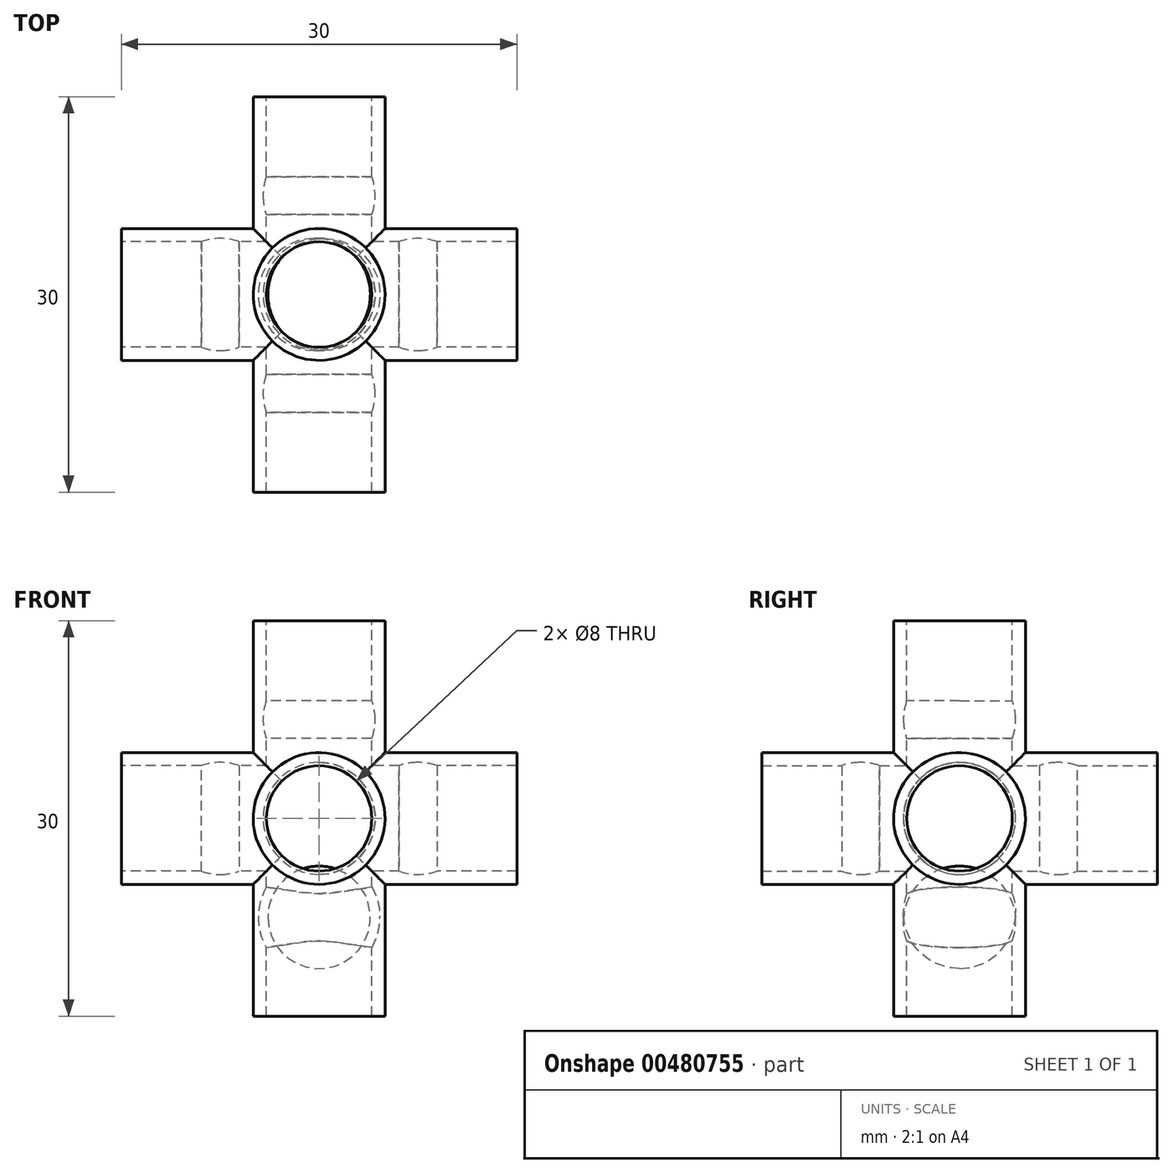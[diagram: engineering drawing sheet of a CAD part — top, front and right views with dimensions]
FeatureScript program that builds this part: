
annotation { "Feature Type Name" : "Feature", "Feature Type Description" : "" }
export const myFeature = defineFeature(function(context is Context, id is Id, definition is map)
    precondition{}
    {
        {
            var Q0;
            Q0=qCreatedBy(makeId("Top.planeOp"),FACE);
            var sketch = newSketch(context, id + "F0", { "sketchPlane" : qUnion([Q0])});
            skCircle(sketch, "E0", {"center": v(0, 0) * mm, "radius": 5 * mm});
            skSolve(sketch);
        }
        {
            var Q0;
            Q0=qCreatedBy(makeId("Right.planeOp"),FACE);
            var sketch = newSketch(context, id + "F1", { "sketchPlane" : qUnion([Q0])});
            skCircle(sketch, "E1", {"center": v(0, 0) * mm, "radius": 5 * mm});
            skSolve(sketch);
        }
        {
            var Q0;
            Q0=qCreatedBy(makeId("Front.planeOp"),FACE);
            var sketch = newSketch(context, id + "F2", { "sketchPlane" : qUnion([Q0])});
            skCircle(sketch, "E2", {"center": v(0, 0) * mm, "radius": 5 * mm});
            skSolve(sketch);
        }
        {
            var Q0;
            Q0 = qSketchRegion(id + "F0", true);
            extrude(context, id + "F3", {"entities" : qUnion([Q0]), "endBound" : BoundingType.SYMMETRIC, "depth" : 30 * mm});
        }
        {
            var Q0;
            Q0 = qSketchRegion(id + "F1", true);
            extrude(context, id + "F4", {"entities" : qUnion([Q0]), "operationType" : NewBodyOperationType.ADD, "endBound" : BoundingType.SYMMETRIC, "depth" : 30 * mm});
        }
        {
            var Q0;
            Q0 = qSketchRegion(id + "F2", true);
            extrude(context, id + "F5", {"entities" : qUnion([Q0]), "operationType" : NewBodyOperationType.ADD, "endBound" : BoundingType.SYMMETRIC, "depth" : 30 * mm});
        }
        {
            var Q0;
            Q0=qCreatedBy(makeId("Top.planeOp"),FACE);
            var sketch = newSketch(context, id + "F6", { "sketchPlane" : qUnion([Q0])});
            skCircle(sketch, "E3", {"center": v(0, 0) * mm, "radius": 4 * mm});
            skSolve(sketch);
        }
        {
            var Q0;
            Q0=qCreatedBy(makeId("Right.planeOp"),FACE);
            var sketch = newSketch(context, id + "F7", { "sketchPlane" : qUnion([Q0])});
            skCircle(sketch, "E4", {"center": v(0, 0) * mm, "radius": 4 * mm});
            skSolve(sketch);
        }
        {
            var Q0;
            Q0=qCreatedBy(makeId("Front.planeOp"),FACE);
            var sketch = newSketch(context, id + "F8", { "sketchPlane" : qUnion([Q0])});
            skCircle(sketch, "E5", {"center": v(0, 0) * mm, "radius": 4 * mm});
            skSolve(sketch);
        }
        {
            var Q0;
            Q0 = qSketchRegion(id + "F6", true);
            extrude(context, id + "F9", {"entities" : qUnion([Q0]), "operationType" : NewBodyOperationType.REMOVE, "endBound" : BoundingType.SYMMETRIC, "oppositeDirection" : true, "depth" : 30 * mm});
        }
        {
            var Q0;
            Q0 = qSketchRegion(id + "F7", true);
            extrude(context, id + "F10", {"entities" : qUnion([Q0]), "operationType" : NewBodyOperationType.REMOVE, "endBound" : BoundingType.SYMMETRIC, "depth" : 30 * mm});
        }
        {
            var Q0;
            Q0 = qSketchRegion(id + "F8", true);
            extrude(context, id + "F11", {"entities" : qUnion([Q0]), "operationType" : NewBodyOperationType.REMOVE, "endBound" : BoundingType.SYMMETRIC, "depth" : 30 * mm});
        }
        {
            var Q0;
            Q0=qCreatedBy(makeId("Front.planeOp"),FACE);
            cPlane(context, id + "F12", {"entities" : qUnion([Q0]), "cplaneType" : CPlaneType.OFFSET, "offset" : 7.5 * mm, "width" : 150 * mm, "height" : 150 * mm});
        }
        {
            var Q0;
            Q0=qCreatedBy(makeId("Front.planeOp"),FACE);
            cPlane(context, id + "F13", {"entities" : qUnion([Q0]), "cplaneType" : CPlaneType.OFFSET, "offset" : 7.5 * mm, "oppositeDirection" : true, "width" : 150 * mm, "height" : 150 * mm});
        }
        {
            var Q0;
            Q0=qCreatedBy(makeId("Top.planeOp"),FACE);
            cPlane(context, id + "F14", {"entities" : qUnion([Q0]), "cplaneType" : CPlaneType.OFFSET, "offset" : 7.5 * mm, "width" : 150 * mm, "height" : 150 * mm});
        }
        {
            var Q0;
            Q0=qCreatedBy(makeId("Top.planeOp"),FACE);
            cPlane(context, id + "F15", {"entities" : qUnion([Q0]), "cplaneType" : CPlaneType.OFFSET, "offset" : 7.5 * mm, "oppositeDirection" : true, "width" : 150 * mm, "height" : 150 * mm});
        }
        {
            var Q0;
            Q0=qCreatedBy(makeId("Right.planeOp"),FACE);
            cPlane(context, id + "F16", {"entities" : qUnion([Q0]), "cplaneType" : CPlaneType.OFFSET, "offset" : 7.5 * mm, "width" : 150 * mm, "height" : 150 * mm});
        }
        {
            var Q0;
            Q0=qCreatedBy(makeId("Right.planeOp"),FACE);
            cPlane(context, id + "F17", {"entities" : qUnion([Q0]), "cplaneType" : CPlaneType.OFFSET, "offset" : 7.5 * mm, "oppositeDirection" : true, "width" : 150 * mm, "height" : 150 * mm});
        }
        {
            var Q0;
            Q0=qCreatedBy(id+"F12.planeOp",FACE);
            var sketch = newSketch(context, id + "F18", { "sketchPlane" : qUnion([Q0])});
            skLineSegment(sketch, "E6", {"start": v(0, 4.25) * mm, "end": v(0, -4.25) * mm});
            skArc(sketch, "E7", {"start": v(0, -4.25) * mm, "mid": v(4.25, 0) * mm, "end": v(0, 4.25) * mm});
            skSolve(sketch);
        }
        {
            var Q0;
            Q0=qCreatedBy(id+"F13.planeOp",FACE);
            var sketch = newSketch(context, id + "F19", { "sketchPlane" : qUnion([Q0])});
            skLineSegment(sketch, "E8", {"start": v(0, 4.25) * mm, "end": v(0, -4.25) * mm});
            skArc(sketch, "E9", {"start": v(0, 4.25) * mm, "mid": v(-4.25, 0) * mm, "end": v(0, -4.25) * mm});
            skSolve(sketch);
        }
        {
            var Q0;
            Q0=qCreatedBy(id+"F14.planeOp",FACE);
            var sketch = newSketch(context, id + "F20", { "sketchPlane" : qUnion([Q0])});
            skLineSegment(sketch, "E10", {"start": v(0, 4.25) * mm, "end": v(0, -4.25) * mm});
            skArc(sketch, "E11", {"start": v(0, -4.25) * mm, "mid": v(4.25, 0) * mm, "end": v(0, 4.25) * mm});
            skSolve(sketch);
        }
        {
            var Q0;
            Q0 = qSketchRegion(id + "F18", true);
            var Q1;
            Q1=sQuery(id+"F18.wireOp",EDGE,"E6");
            revolve(context, id + "F21", {"operationType" : NewBodyOperationType.REMOVE, "entities" : qUnion([Q0]), "axis" : qUnion([Q1]), "revolveType" : RevolveType.FULL, "oppositeDirection" : true});
        }
        {
            var Q0;
            Q0 = qSketchRegion(id + "F19", true);
            var Q1;
            Q1=sQuery(id+"F19.wireOp",EDGE,"E8");
            revolve(context, id + "F22", {"operationType" : NewBodyOperationType.REMOVE, "entities" : qUnion([Q0]), "axis" : qUnion([Q1]), "revolveType" : RevolveType.FULL});
        }
        {
            var Q0;
            Q0 = qSketchRegion(id + "F20", true);
            var Q1;
            Q1=sQuery(id+"F20.wireOp",EDGE,"E10");
            revolve(context, id + "F23", {"operationType" : NewBodyOperationType.REMOVE, "entities" : qUnion([Q0]), "axis" : qUnion([Q1]), "revolveType" : RevolveType.FULL, "oppositeDirection" : true});
        }
        {
            var Q0;
            Q0=qCreatedBy(id+"F15.planeOp",FACE);
            var sketch = newSketch(context, id + "F24", { "sketchPlane" : qUnion([Q0])});
            skLineSegment(sketch, "E12", {"start": v(0, 4.23) * mm, "end": v(0, -4.23) * mm});
            skArc(sketch, "E13", {"start": v(0, 4.23) * mm, "mid": v(-4.61, 0) * mm, "end": v(0, -4.23) * mm});
            skPoint(sketch, "E13.centerSnap0", {"position": v(0, 0) * mm});
            skSolve(sketch);
        }
        {
            var Q0;
            Q0 = qSketchRegion(id + "F24", true);
            var Q1;
            Q1=sQuery(id+"F24.wireOp",EDGE,"E12");
            revolve(context, id + "F25", {"operationType" : NewBodyOperationType.REMOVE, "entities" : qUnion([Q0]), "axis" : qUnion([Q1]), "revolveType" : RevolveType.FULL, "oppositeDirection" : true});
        }
        {
            var Q0;
            Q0=qCreatedBy(id+"F16.planeOp",FACE);
            var sketch = newSketch(context, id + "F26", { "sketchPlane" : qUnion([Q0])});
            skLineSegment(sketch, "E14", {"start": v(-2.62, -3.34) * mm, "end": v(2.62, 3.34) * mm});
            skArc(sketch, "E15", {"start": v(-2.62, -3.34) * mm, "mid": v(3.34, -2.62) * mm, "end": v(2.62, 3.34) * mm});
            skSolve(sketch);
        }
        {
            var Q0;
            Q0 = qSketchRegion(id + "F26", true);
            var Q1;
            Q1=sQuery(id+"F26.wireOp",EDGE,"E14");
            revolve(context, id + "F27", {"operationType" : NewBodyOperationType.REMOVE, "entities" : qUnion([Q0]), "axis" : qUnion([Q1]), "revolveType" : RevolveType.FULL, "oppositeDirection" : true});
        }
        {
            var Q0;
            Q0=qCreatedBy(id+"F17.planeOp",FACE);
            var sketch = newSketch(context, id + "F28", { "sketchPlane" : qUnion([Q0])});
            skLineSegment(sketch, "E16", {"start": v(-2.84, 3.16) * mm, "end": v(2.84, -3.16) * mm});
            skArc(sketch, "E17", {"start": v(2.84, -3.16) * mm, "mid": v(3.16, 2.84) * mm, "end": v(-2.84, 3.16) * mm});
            skSolve(sketch);
        }
        {
            var Q0;
            Q0 = qSketchRegion(id + "F28", true);
            var Q1;
            Q1=sQuery(id+"F28.wireOp",EDGE,"E16");
            revolve(context, id + "F29", {"operationType" : NewBodyOperationType.REMOVE, "entities" : qUnion([Q0]), "axis" : qUnion([Q1]), "revolveType" : RevolveType.FULL, "oppositeDirection" : true});
        }
    });
